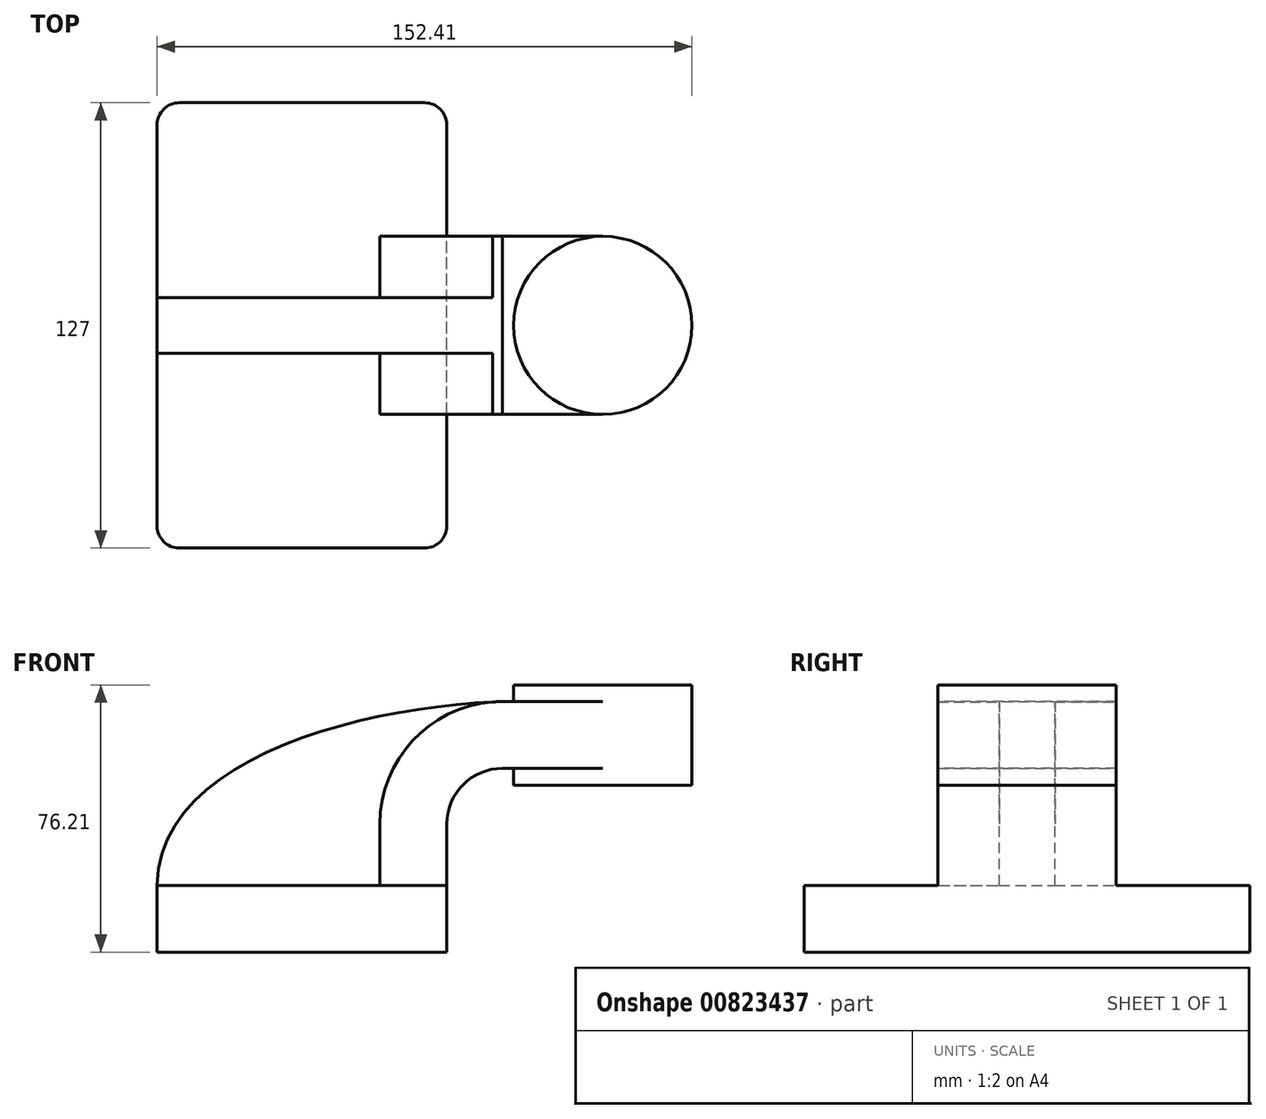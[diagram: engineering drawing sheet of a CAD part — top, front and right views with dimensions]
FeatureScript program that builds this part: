
annotation { "Feature Type Name" : "Feature", "Feature Type Description" : "" }
export const myFeature = defineFeature(function(context is Context, id is Id, definition is map)
    precondition{}
    {
        {
            var Q0;
            Q0=qCreatedBy(makeId("Front.planeOp"),FACE);
            var sketch = newSketch(context, id + "F0", { "sketchPlane" : qUnion([Q0])});
            skLineSegment(sketch, "E0.bottom", {"start": v(-41.28, -9.53) * mm, "end": v(41.28, -9.53) * mm});
            skLineSegment(sketch, "E0.top", {"start": v(-41.28, 9.52) * mm, "end": v(41.28, 9.52) * mm});
            skLineSegment(sketch, "E0.left", {"start": v(-41.28, -9.53) * mm, "end": v(-41.28, 9.52) * mm});
            skLineSegment(sketch, "E0.right", {"start": v(41.28, -9.53) * mm, "end": v(41.28, 9.52) * mm});
            skPoint(sketch, "E0.middle", {"position": v(0, 0) * mm});
            skLineSegment(sketch, "E1.bottom", {"start": v(60.32, 38.1) * mm, "end": v(111.12, 38.1) * mm});
            skLineSegment(sketch, "E1.top", {"start": v(60.32, 66.67) * mm, "end": v(111.12, 66.67) * mm});
            skLineSegment(sketch, "E1.left", {"start": v(60.32, 38.1) * mm, "end": v(60.32, 66.67) * mm});
            skLineSegment(sketch, "E1.right", {"start": v(111.12, 38.1) * mm, "end": v(111.12, 66.67) * mm});
            skPoint(sketch, "E1.middle", {"position": v(85.72, 52.39) * mm});
            skLineSegment(sketch, "E2", {"start": v(41.28, 9.52) * mm, "end": v(41.28, 27) * mm});
            skArc(sketch, "E3", {"start": v(41.27, 27) * mm, "mid": v(45.92, 38.23) * mm, "end": v(57.15, 42.88) * mm});
            skLineSegment(sketch, "E4", {"start": v(57.15, 42.88) * mm, "end": v(85.72, 42.88) * mm});
            skLineSegment(sketch, "E5.0", {"start": v(57.15, 61.93) * mm, "end": v(85.72, 61.93) * mm});
            skArc(sketch, "E5.1", {"start": v(22.22, 27) * mm, "mid": v(32.45, 51.7) * mm, "end": v(57.15, 61.93) * mm});
            skLineSegment(sketch, "E5.2", {"start": v(22.22, 9.52) * mm, "end": v(22.22, 27) * mm});
            skFitSpline(sketch, "E6", {"points": [v(-41.28, 9.53) * mm, v(57.15, 61.93) * mm], "startDerivative": vector(1.7, 111.38) * mm, "endDerivative": vector(114.65, 3.76) * mm});
            skLineSegment(sketch, "E7", {"start": v(85.72, 66.67) * mm, "end": v(85.72, 38.1) * mm});
            skSolve(sketch);
        }
        {
            var Q0;
            Q0=makeQuery(id+"F0.imprint","IMPRINT",FACE,{"disambiguationData":[TD([[makeQuery(id+"F0.imprint","IMPRINT",EDGE,{"derivedFrom":sQuery(id+"F0.wireOp",EDGE,"E0.bottom")}),1.0]])]});
            extrude(context, id + "F1", {"entities" : qUnion([Q0]), "endBound" : BoundingType.SYMMETRIC, "depth" : 127 * mm, "offsetDistance" : 25.4 * mm});
        }
        {
            var Q0;
            {var subQ0=sQuery(id+"F0.wireOp",EDGE,"E2");Q0=makeQuery(id+"F0.imprint","IMPRINT",FACE,{"disambiguationData":[TD([[makeQuery(id+"F0.imprint","IMPRINT",EDGE,{"derivedFrom":subQ0}),1.0]])]});}
            var Q1;
            {var subQ0=sQuery(id+"F0.wireOp",EDGE,"E4");var subQ1=sQuery(id+"F0.wireOp",EDGE,"E1.left");var subQ2=makeQuery(id+"F0.imprint","INTERSECT",VERTEX,{"derivedFrom":[subQ1,subQ0]});Q1=makeQuery(id+"F0.imprint","IMPRINT",FACE,{"disambiguationData":[TD([[makeQuery(id+"F0.imprint","IMPRINT",EDGE,{"disambiguationData":[TD([[subQ2,-1.0]])],"derivedFrom":subQ1}),-1.0]])]});}
            extrude(context, id + "F2", {"entities" : qUnion([Q0, Q1]), "operationType" : NewBodyOperationType.ADD, "endBound" : BoundingType.SYMMETRIC, "depth" : 50.8 * mm, "offsetDistance" : 25.4 * mm});
        }
        {
            var Q0;
            {var subQ3=sQuery(id+"F0.wireOp",EDGE,"E5.2");Q0=makeQuery(id+"F0.imprint","IMPRINT",FACE,{"disambiguationData":[TD([[makeQuery(id+"F0.imprint","IMPRINT",EDGE,{"derivedFrom":subQ3}),1.0]])]});}
            extrude(context, id + "F3", {"entities" : qUnion([Q0]), "operationType" : NewBodyOperationType.ADD, "endBound" : BoundingType.SYMMETRIC, "depth" : 15.88 * mm, "offsetDistance" : 25.4 * mm});
        }
        {
            var Q0;
            {var subQ4=sQuery(id+"F0.wireOp",EDGE,"E1.right");Q0=makeQuery(id+"F0.imprint","IMPRINT",FACE,{"disambiguationData":[TD([[makeQuery(id+"F0.imprint","IMPRINT",EDGE,{"derivedFrom":subQ4}),1.0]])]});}
            var Q1;
            Q1=sQuery(id+"F0.wireOp",EDGE,"E7");
            revolve(context, id + "F4", {"operationType" : NewBodyOperationType.ADD, "surfaceOperationType" : NewSurfaceOperationType.NEW, "entities" : qUnion([Q0]), "axis" : qUnion([Q1]), "revolveType" : RevolveType.FULL});
        }
        {
            var Q0;
            Q0=makeQuery(id+"F1.opExtrude","CAP_EDGE",EDGE,{"disambiguationData":[OSD([sQuery(id+"F0.wireOp",EDGE,"E0.left")])],"isStart":false});
            var Q1;
            Q1=makeQuery(id+"F1.opExtrude","CAP_EDGE",EDGE,{"disambiguationData":[OSD([sQuery(id+"F0.wireOp",EDGE,"E0.right")])],"isStart":false});
            var Q2;
            Q2=makeQuery(id+"F1.opExtrude","CAP_EDGE",EDGE,{"disambiguationData":[OSD([sQuery(id+"F0.wireOp",EDGE,"E0.right")])],"isStart":true});
            var Q3;
            Q3=makeQuery(id+"F1.opExtrude","CAP_EDGE",EDGE,{"disambiguationData":[OSD([sQuery(id+"F0.wireOp",EDGE,"E0.left")])],"isStart":true});
            fillet(context, id + "F5", {"entities" : qUnion([Q0, Q1, Q2, Q3]), "radius" : 6.35 * mm, "tangentPropagation" : true, "allowEdgeOverflow" : false});
        }
    });
